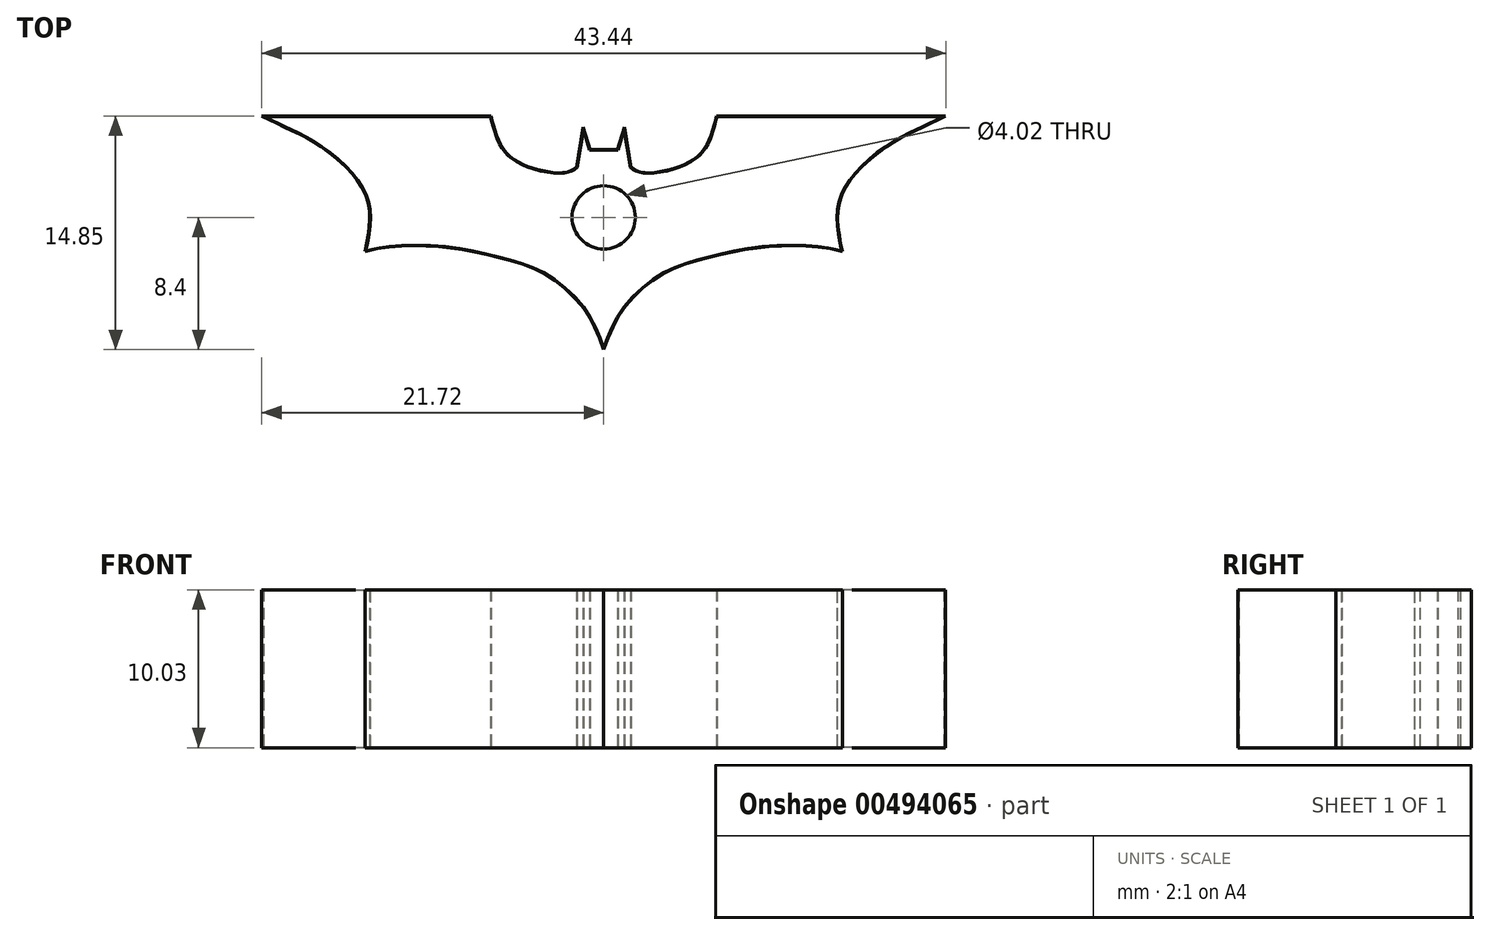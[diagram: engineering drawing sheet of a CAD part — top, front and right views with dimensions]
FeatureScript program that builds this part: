
annotation { "Feature Type Name" : "Feature", "Feature Type Description" : "" }
export const myFeature = defineFeature(function(context is Context, id is Id, definition is map)
    precondition{}
    {
        {
            var Q0;
            Q0=qCreatedBy(makeId("Top.planeOp"),FACE);
            var sketch = newSketch(context, id + "F0", { "sketchPlane" : qUnion([Q0])});
            skLineSegment(sketch, "E0", {"start": v(-21.6, 6.42) * mm, "end": v(-7.19, 6.42) * mm});
            skLineSegment(sketch, "E1", {"start": v(-1.3, 5.6) * mm, "end": v(-1.7, 3.16) * mm});
            skLineSegment(sketch, "E2", {"start": v(-1.3, 5.6) * mm, "end": v(-0.9, 4.29) * mm});
            skLineSegment(sketch, "E3", {"start": v(-0.9, 4.29) * mm, "end": v(0, 4.29) * mm});
            skFitSpline(sketch, "E4", {"points": [v(-7.19, 6.42) * mm, v(-6.64, 4.72) * mm, v(-5.36, 3.44) * mm, v(-2.59, 2.81) * mm, v(-1.7, 3.16) * mm], "startDerivative": vector(1.72, -7.12) * mm, "endDerivative": vector(3.88, 2.52) * mm});
            skFitSpline(sketch, "E5", {"points": [v(-21.6, 6.42) * mm, v(-20.57, 5.91) * mm, v(-18.48, 4.87) * mm, v(-15.8, 2.6) * mm, v(-14.85, 0.43) * mm, v(-15.11, -2.14) * mm], "startDerivative": vector(6.7, -3.43) * mm, "endDerivative": vector(-2.5, -12.52) * mm});
            skFitSpline(sketch, "E6", {"points": [v(-15.11, -2.14) * mm, v(-14.04, -1.9) * mm, v(-10.28, -1.84) * mm, v(-6.55, -2.56) * mm, v(-3.8, -3.51) * mm, v(-1.15, -5.9) * mm, v(0, -8.31) * mm], "startDerivative": vector(8.65, 2.5) * mm, "endDerivative": vector(5.49, -15.07) * mm});
            skLineSegment(sketch, "E7.MirrorCS", {"start": v(0.9, 4.29) * mm, "end": v(0, 4.29) * mm});
            skLineSegment(sketch, "E8.MirrorCS", {"start": v(1.3, 5.6) * mm, "end": v(1.7, 3.16) * mm});
            skFitSpline(sketch, "E9.MirrorCS", {"points": [v(21.6, 6.42) * mm, v(20.57, 5.91) * mm, v(18.48, 4.87) * mm, v(15.8, 2.6) * mm, v(14.85, 0.43) * mm, v(15.11, -2.14) * mm], "startDerivative": vector(-6.7, -3.43) * mm, "endDerivative": vector(2.5, -12.52) * mm});
            skFitSpline(sketch, "E10.MirrorCS", {"points": [v(15.11, -2.14) * mm, v(14.04, -1.9) * mm, v(10.28, -1.84) * mm, v(6.55, -2.56) * mm, v(3.8, -3.51) * mm, v(1.15, -5.9) * mm, v(0, -8.31) * mm], "startDerivative": vector(-8.65, 2.5) * mm, "endDerivative": vector(-5.49, -15.07) * mm});
            skLineSegment(sketch, "E11.MirrorCS", {"start": v(1.3, 5.6) * mm, "end": v(0.9, 4.29) * mm});
            skLineSegment(sketch, "E12.MirrorCS", {"start": v(21.6, 6.42) * mm, "end": v(7.19, 6.42) * mm});
            skFitSpline(sketch, "E13.MirrorCS", {"points": [v(7.19, 6.42) * mm, v(6.64, 4.72) * mm, v(5.36, 3.44) * mm, v(2.59, 2.81) * mm, v(1.7, 3.16) * mm], "startDerivative": vector(-1.72, -7.12) * mm, "endDerivative": vector(-3.88, 2.52) * mm});
            skSolve(sketch);
        }
        {
            var Q0;
            Q0=makeQuery(id+"F0.imprint","IMPRINT",FACE,{"disambiguationData":[TD([[makeQuery(id+"F0.imprint","IMPRINT",EDGE,{"derivedFrom":sQuery(id+"F0.wireOp",EDGE,"E0")}),-1.0]])]});
            extrude(context, id + "F1", {"entities" : qUnion([Q0]), "depth" : 10 * mm});
        }
        {
            var Q0;
            Q0=makeQuery(id+"F1.opExtrude","CAP_FACE",FACE,{"disambiguationData":[OSD([sQuery(id+"F0.wireOp",EDGE,"E0"),sQuery(id+"F0.wireOp",EDGE,"E1"),sQuery(id+"F0.wireOp",EDGE,"E2"),sQuery(id+"F0.wireOp",EDGE,"E3"),sQuery(id+"F0.wireOp",EDGE,"E4"),sQuery(id+"F0.wireOp",EDGE,"E5"),sQuery(id+"F0.wireOp",EDGE,"E6"),sQuery(id+"F0.wireOp",EDGE,"E7.MirrorCS"),sQuery(id+"F0.wireOp",EDGE,"E8.MirrorCS"),sQuery(id+"F0.wireOp",EDGE,"E9.MirrorCS"),sQuery(id+"F0.wireOp",EDGE,"E10.MirrorCS"),sQuery(id+"F0.wireOp",EDGE,"E11.MirrorCS"),sQuery(id+"F0.wireOp",EDGE,"E12.MirrorCS"),sQuery(id+"F0.wireOp",EDGE,"E13.MirrorCS")])],"isStart":false});
            shell(context, id + "F2", {"entities" : qUnion([Q0]), "thickness" : 0.03 * mm, "oppositeDirection" : true});
        }
        {
            var Q0;
            Q0=qCreatedBy(makeId("Top.planeOp"),FACE);
            var sketch = newSketch(context, id + "F3", { "sketchPlane" : qUnion([Q0])});
            skCircle(sketch, "E14", {"center": v(0, 0) * mm, "radius": 2 * mm});
            skSolve(sketch);
        }
        {
            var Q0;
            Q0 = qSketchRegion(id + "F3", true);
            extrude(context, id + "F4", {"entities" : qUnion([Q0]), "operationType" : NewBodyOperationType.REMOVE, "oppositeDirection" : true, "depth" : 1 * mm});
        }
    });
